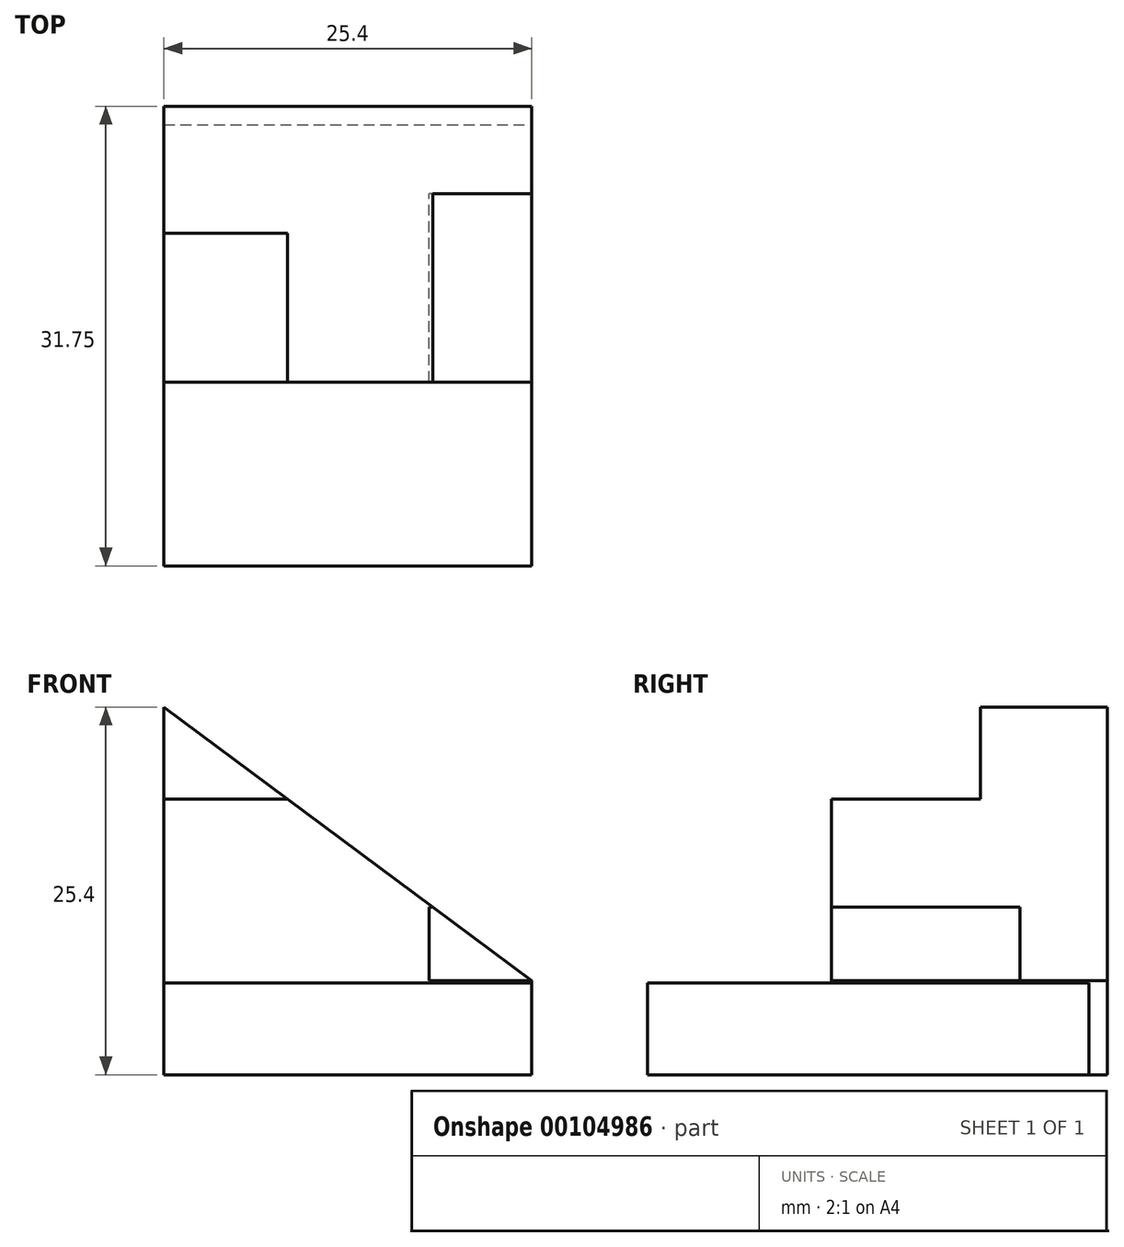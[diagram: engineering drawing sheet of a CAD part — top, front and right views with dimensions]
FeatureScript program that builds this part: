
annotation { "Feature Type Name" : "Feature", "Feature Type Description" : "" }
export const myFeature = defineFeature(function(context is Context, id is Id, definition is map)
    precondition{}
    {
        {
            var Q0;
            Q0=qCreatedBy(makeId("Front.planeOp"),FACE);
            var sketch = newSketch(context, id + "F0", { "sketchPlane" : qUnion([Q0])});
            skLineSegment(sketch, "E0", {"start": v(0, 0) * mm, "end": v(0, 6.35) * mm});
            skPoint(sketch, "E1.end.orphan", {"position": v(0, 25.4) * mm});
            skPoint(sketch, "E2.end.orphan", {"position": v(25.4, 0) * mm});
            skLineSegment(sketch, "E3.top", {"start": v(0, 0) * mm, "end": v(25.4, 0) * mm});
            skLineSegment(sketch, "E3.left", {"start": v(0, 19.05) * mm, "end": v(0, 0) * mm});
            skLineSegment(sketch, "E3.right", {"start": v(25.4, 6.35) * mm, "end": v(25.4, 0) * mm});
            skLineSegment(sketch, "E4", {"start": v(0, 19.05) * mm, "end": v(8.47, 19.05) * mm});
            skLineSegment(sketch, "E5", {"start": v(8.47, 19.05) * mm, "end": v(25.4, 6.35) * mm});
            skSolve(sketch);
        }
        {
            var Q0;
            Q0=qCreatedBy(makeId("Right.planeOp"),FACE);
            var sketch = newSketch(context, id + "F1", { "sketchPlane" : qUnion([Q0])});
            skLineSegment(sketch, "E6", {"start": v(0, 0) * mm, "end": v(31.75, 0) * mm});
            skLineSegment(sketch, "E7", {"start": v(31.75, 0) * mm, "end": v(31.75, 25.4) * mm});
            skLineSegment(sketch, "E8", {"start": v(31.75, 25.4) * mm, "end": v(22.98, 25.4) * mm});
            skLineSegment(sketch, "E9", {"start": v(22.98, 25.4) * mm, "end": v(22.98, 19.05) * mm});
            skLineSegment(sketch, "E10", {"start": v(22.98, 19.05) * mm, "end": v(12.7, 19.05) * mm});
            skLineSegment(sketch, "E11", {"start": v(12.7, 19.05) * mm, "end": v(12.7, 6.35) * mm});
            skLineSegment(sketch, "E12", {"start": v(12.7, 6.35) * mm, "end": v(12.7, 12.7) * mm});
            skLineSegment(sketch, "E13", {"start": v(12.7, 12.7) * mm, "end": v(25.4, 12.7) * mm});
            skLineSegment(sketch, "E14", {"start": v(25.4, 12.7) * mm, "end": v(25.4, 6.35) * mm});
            skLineSegment(sketch, "E15", {"start": v(25.4, 6.35) * mm, "end": v(0, 6.35) * mm});
            skLineSegment(sketch, "E16", {"start": v(0, 6.35) * mm, "end": v(0, 0) * mm});
            skLineSegment(sketch, "E17", {"start": v(25.4, 6.35) * mm, "end": v(31.75, 6.35) * mm});
            skSolve(sketch);
        }
        {
            var Q0;
            Q0 = qSketchRegion(id + "F1", true);
            extrude(context, id + "F2", {"entities" : qUnion([Q0]), "depth" : 25.4 * mm});
        }
        {
            var Q0;
            Q0=qCreatedBy(makeId("Front.planeOp"),FACE);
            var sketch = newSketch(context, id + "F3", { "sketchPlane" : qUnion([Q0])});
            skLineSegment(sketch, "E18", {"start": v(0, 25.4) * mm, "end": v(25.4, 6.5) * mm});
            skLineSegment(sketch, "E19", {"start": v(0, 25.4) * mm, "end": v(25.4, 25.4) * mm});
            skLineSegment(sketch, "E20", {"start": v(25.4, 25.4) * mm, "end": v(25.4, 6.5) * mm});
            skSolve(sketch);
        }
        {
            var Q0;
            Q0 = qSketchRegion(id + "F3", true);
            extrude(context, id + "F4", {"entities" : qUnion([Q0]), "operationType" : NewBodyOperationType.REMOVE, "oppositeDirection" : true, "depth" : 31.75 * mm});
        }
        {
            var Q0;
            Q0=qCreatedBy(makeId("Top.planeOp"),FACE);
            var sketch = newSketch(context, id + "F5", { "sketchPlane" : qUnion([Q0])});
            skLineSegment(sketch, "E21.bottom", {"start": v(0, 0) * mm, "end": v(25.4, 0) * mm});
            skLineSegment(sketch, "E21.top", {"start": v(0, 30.48) * mm, "end": v(25.4, 30.48) * mm});
            skLineSegment(sketch, "E21.left", {"start": v(0, 0) * mm, "end": v(0, 30.48) * mm});
            skLineSegment(sketch, "E21.right", {"start": v(25.4, 0) * mm, "end": v(25.4, 30.48) * mm});
            skLineSegment(sketch, "E22.top", {"start": v(0, 22.61) * mm, "end": v(25.4, 22.61) * mm});
            skLineSegment(sketch, "E22.left", {"start": v(0, 30.48) * mm, "end": v(0, 22.61) * mm});
            skLineSegment(sketch, "E22.right", {"start": v(25.4, 30.48) * mm, "end": v(25.4, 22.61) * mm});
            skLineSegment(sketch, "E23.top", {"start": v(0, 12.65) * mm, "end": v(25.4, 12.65) * mm});
            skLineSegment(sketch, "E23.left", {"start": v(0, 30.48) * mm, "end": v(0, 12.65) * mm});
            skLineSegment(sketch, "E23.right", {"start": v(25.4, 30.48) * mm, "end": v(25.4, 12.65) * mm});
            skSolve(sketch);
        }
        {
            var Q0;
            Q0 = qSketchRegion(id + "F5", true);
            extrude(context, id + "F6", {"entities" : qUnion([Q0]), "depth" : 6.35 * mm});
        }
        {
            var Q0;
            Q0=qCreatedBy(makeId("Right.planeOp"),FACE);
            var sketch = newSketch(context, id + "F7", { "sketchPlane" : qUnion([Q0])});
            skLineSegment(sketch, "E24.bottom", {"start": v(12.09, 6.5) * mm, "end": v(25.7, 6.5) * mm});
            skLineSegment(sketch, "E24.top", {"start": v(12.09, 11.57) * mm, "end": v(25.7, 11.57) * mm});
            skLineSegment(sketch, "E24.left", {"start": v(12.09, 6.5) * mm, "end": v(12.09, 11.57) * mm});
            skLineSegment(sketch, "E24.right", {"start": v(25.7, 6.5) * mm, "end": v(25.7, 11.57) * mm});
            skSolve(sketch);
        }
        {
            var Q0;
            Q0 = qSketchRegion(id + "F7", true);
            extrude(context, id + "F8", {"entities" : qUnion([Q0]), "operationType" : NewBodyOperationType.REMOVE, "depth" : 25.4 * mm, "hasSecondDirection" : true, "secondDirectionOppositeDirection" : false, "secondDirectionDepth" : 18.33 * mm});
        }
    });
